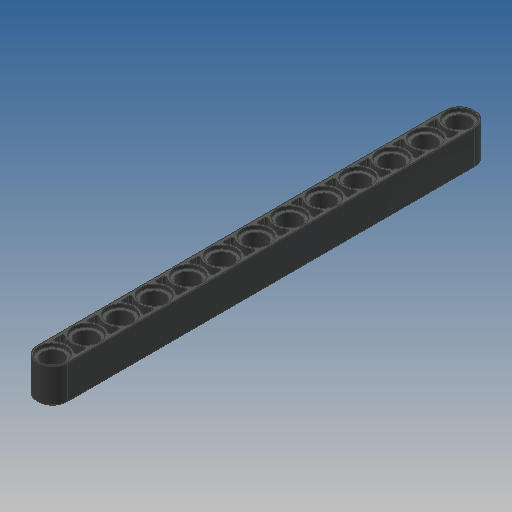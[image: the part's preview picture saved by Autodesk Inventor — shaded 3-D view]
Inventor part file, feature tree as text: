
AUTODESK INVENTOR PART (.ipt)
format: ipt  version: 2022.2 (Build 262287000, 287)  size: 497,152 bytes
history: native  units: mm
features: extrude x3, sketch x2, projected_geometry x2, mirror x1, fillet x1
ambient origin geometry x8: Origin, YZ Plane, XZ Plane, XY Plane, X Axis, Y Axis, Z Axis, Center Point
bodies: Solid1 (feature_tree)
feature tree (9):
  extrude  "Extrusion1"  Depth=7.2mm
  sketch  "Sketch6"  dims[d41=0.8mm d42=0.0mm d43=3.1mm d44=0.0mm d48=96.0mm d49=6.4mm d50=4.8mm d51=8.0mm d52=0.8mm d53=120.0mm d55=8.0mm d56=10.0mm d58=10.0mm d60=0.4mm d61=0.1mm]
  extrude  "Extrusion7"  Depth=3.1mm TaperAngle=0.0deg
  extrude  "Extrusion8"  Depth=0.1mm
  mirror  "Mirror1"
  fillet  "Fillet2"  Radius=6.4mm
  sketch  "Sketch1"  dims[d14=8.0mm d15=0.0mm d32=7.2mm]
  projected_geometry  "Projected Loop3"
  projected_geometry  "Projected Loop4"
